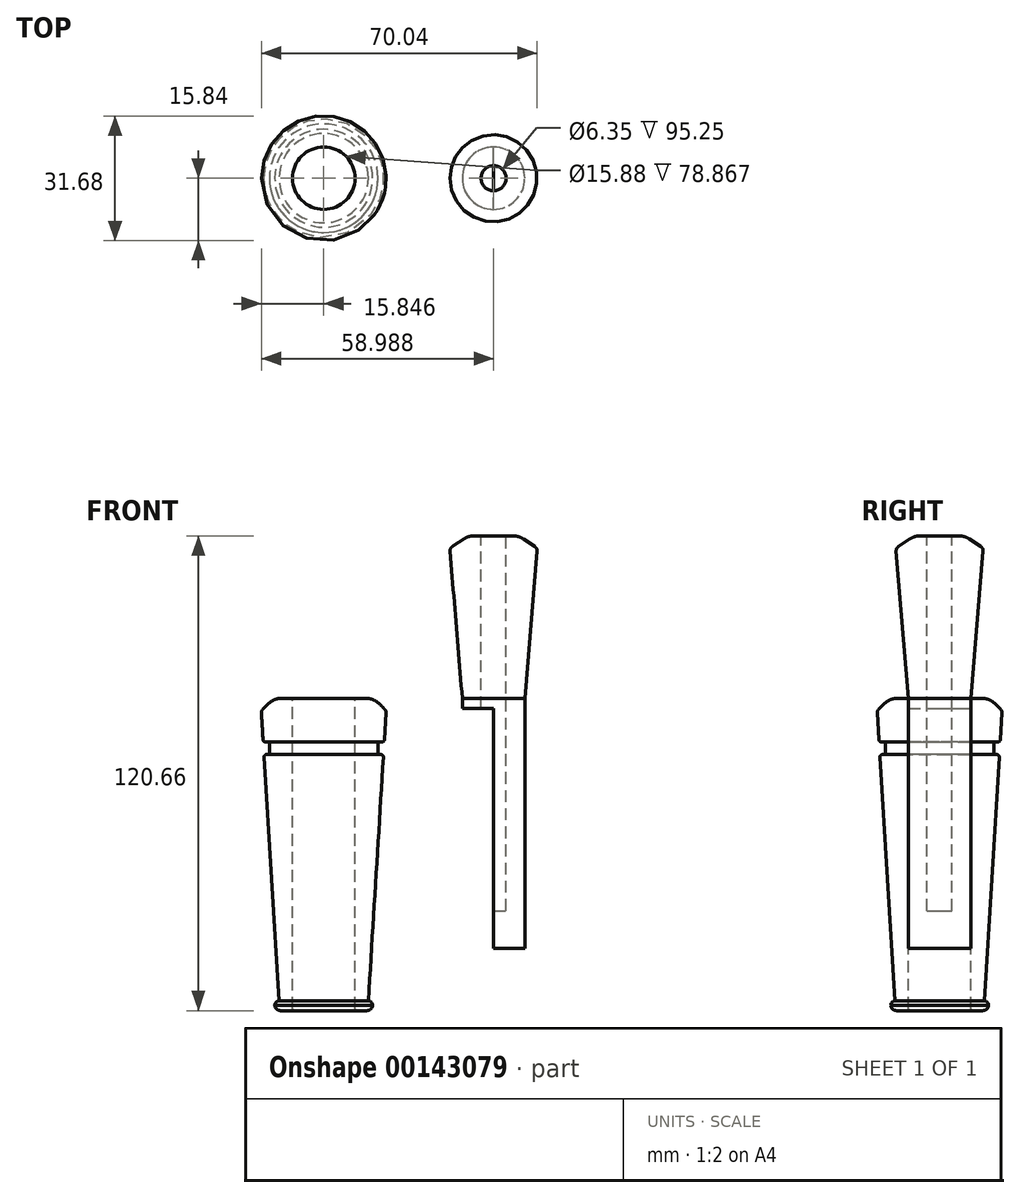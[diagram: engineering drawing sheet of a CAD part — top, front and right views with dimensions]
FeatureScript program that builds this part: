
annotation { "Feature Type Name" : "Feature", "Feature Type Description" : "" }
export const myFeature = defineFeature(function(context is Context, id is Id, definition is map)
    precondition{}
    {
        {
            var Q0;
            Q0=qCreatedBy(makeId("Front.planeOp"),FACE);
            var sketch = newSketch(context, id + "F0", { "sketchPlane" : qUnion([Q0])});
            skLineSegment(sketch, "E0", {"start": v(-45.17, -3.17) * mm, "end": v(-29.3, -3.17) * mm});
            skLineSegment(sketch, "E1", {"start": v(-29.3, -3.17) * mm, "end": v(-29.3, -79.38) * mm});
            skLineSegment(sketch, "E2", {"start": v(-29.3, -79.38) * mm, "end": v(-40.47, -79.38) * mm});
            skLineSegment(sketch, "E3", {"start": v(-45.17, -3.18) * mm, "end": v(-44.68, -11.11) * mm});
            skLineSegment(sketch, "E4", {"start": v(-40.47, -79.38) * mm, "end": v(-41.74, -79.38) * mm});
            skLineSegment(sketch, "E5", {"start": v(-41.74, -79.38) * mm, "end": v(-41.74, -76.83) * mm});
            skLineSegment(sketch, "E6", {"start": v(-41.74, -76.83) * mm, "end": v(-29.3, -76.83) * mm});
            skLineSegment(sketch, "E7", {"start": v(-29.3, -3.17) * mm, "end": v(-29.3, 0) * mm});
            skLineSegment(sketch, "E8", {"start": v(-29.3, 0) * mm, "end": v(-42, 0) * mm});
            skLineSegment(sketch, "E9", {"start": v(-42, 0) * mm, "end": v(-45.17, -3.18) * mm});
            skLineSegment(sketch, "E10", {"start": v(-29.3, -3.17) * mm, "end": v(-29.3, -12.7) * mm});
            skLineSegment(sketch, "E11", {"start": v(-29.3, -12.7) * mm, "end": v(-43.1, -12.7) * mm});
            skLineSegment(sketch, "E12", {"start": v(-44.68, -11.11) * mm, "end": v(-43.1, -11.11) * mm});
            skLineSegment(sketch, "E13", {"start": v(-44.48, -14.29) * mm, "end": v(-43.1, -14.29) * mm});
            skLineSegment(sketch, "E14", {"start": v(-43.1, -11.11) * mm, "end": v(-43.1, -14.29) * mm});
            skLineSegment(sketch, "E15.trimOffspring", {"start": v(-44.48, -14.29) * mm, "end": v(-40.47, -79.38) * mm});
            skLineSegment(sketch, "E16", {"start": v(-29.3, 6.8) * mm, "end": v(-37.23, 6.8) * mm, "construction": true});
            skLineSegment(sketch, "E17", {"start": v(-37.23, 6.8) * mm, "end": v(-37.23, -111.45) * mm, "construction": true});
            skLineSegment(sketch, "E18", {"start": v(-37.23, -76.83) * mm, "end": v(-40.63, -76.83) * mm, "construction": true});
            skSolve(sketch);
        }
        {
            var Q0;
            Q0=makeQuery(id+"F0.imprint","IMPRINT",FACE,{"disambiguationData":[TD([[makeQuery(id+"F0.imprint","IMPRINT",EDGE,{"derivedFrom":sQuery(id+"F0.wireOp",EDGE,"E0")}),1.0]])]});
            var Q1;
            Q1=makeQuery(id+"F0.imprint","IMPRINT",FACE,{"disambiguationData":[TD([[makeQuery(id+"F0.imprint","IMPRINT",EDGE,{"derivedFrom":sQuery(id+"F0.wireOp",EDGE,"E0")}),-1.0]])]});
            var Q2;
            {var subQ1=sQuery(id+"F0.wireOp",EDGE,"E11");Q2=makeQuery(id+"F0.imprint","IMPRINT",FACE,{"disambiguationData":[TD([[makeQuery(id+"F0.imprint","IMPRINT",EDGE,{"derivedFrom":subQ1}),1.0]])]});}
            var Q3;
            {var subQ0=sQuery(id+"F0.wireOp",EDGE,"E2");Q3=makeQuery(id+"F0.imprint","IMPRINT",FACE,{"disambiguationData":[TD([[makeQuery(id+"F0.imprint","IMPRINT",EDGE,{"derivedFrom":subQ0}),-1.0]])]});}
            var Q4;
            {var subQ0=sQuery(id+"F0.wireOp",EDGE,"E4");Q4=makeQuery(id+"F0.imprint","IMPRINT",FACE,{"disambiguationData":[TD([[makeQuery(id+"F0.imprint","IMPRINT",EDGE,{"derivedFrom":subQ0}),-1.0]])]});}
            var Q5;
            Q5=sQuery(id+"F0.wireOp",EDGE,"E1");
            revolve(context, id + "F1", {"entities" : qUnion([Q0, Q1, Q2, Q3, Q4]), "axis" : qUnion([Q5]), "revolveType" : RevolveType.FULL});
        }
        {
            var Q0;
            Q0=makeQuery(id+"F1.opRevolve","SWEPT_FACE",FACE,{"disambiguationData":[OSD([sQuery(id+"F0.wireOp",EDGE,"E8")])]});
            var sketch = newSketch(context, id + "F2", { "sketchPlane" : qUnion([Q0])});
            skCircle(sketch, "E19", {"center": v(-29.3, 0) * mm, "radius": 7.94 * mm});
            skSolve(sketch);
        }
        {
            var Q0;
            Q0 = qSketchRegion(id + "F2", true);
            extrude(context, id + "F3", {"entities" : qUnion([Q0]), "operationType" : NewBodyOperationType.REMOVE, "endBound" : BoundingType.THROUGH_ALL, "oppositeDirection" : true, "depth" : 25.4 * mm});
        }
        {
            var Q0;
            Q0=qCreatedBy(makeId("Front.planeOp"),FACE);
            var sketch = newSketch(context, id + "F4", { "sketchPlane" : qUnion([Q0])});
            skLineSegment(sketch, "E20", {"start": v(13.85, 0) * mm, "end": v(13.85, 38.1) * mm});
            skLineSegment(sketch, "E21", {"start": v(13.85, 38.1) * mm, "end": v(13.85, 41.27) * mm});
            skLineSegment(sketch, "E22", {"start": v(13.85, 41.27) * mm, "end": v(7.5, 41.27) * mm});
            skLineSegment(sketch, "E23", {"start": v(5.91, 0) * mm, "end": v(5.91, -63.5) * mm});
            skLineSegment(sketch, "E24", {"start": v(13.85, 0) * mm, "end": v(13.85, -63.5) * mm});
            skLineSegment(sketch, "E25", {"start": v(13.85, -63.5) * mm, "end": v(5.91, -63.5) * mm});
            skLineSegment(sketch, "E26", {"start": v(13.85, 38.1) * mm, "end": v(2.74, 38.1) * mm});
            skLineSegment(sketch, "E27", {"start": v(5.91, 0) * mm, "end": v(2.74, 38.1) * mm});
            skLineSegment(sketch, "E28", {"start": v(2.74, 38.1) * mm, "end": v(7.5, 41.27) * mm});
            skSolve(sketch);
        }
        {
            var Q0;
            Q0 = qSketchRegion(id + "F4", true);
            var Q1;
            Q1=sQuery(id+"F4.wireOp",EDGE,"E20");
            revolve(context, id + "F5", {"entities" : qUnion([Q0]), "axis" : qUnion([Q1]), "revolveType" : RevolveType.FULL});
        }
        {
            var Q0;
            Q0=makeQuery(id+"F5.opRevolve","SWEPT_FACE",FACE,{"disambiguationData":[OSD([sQuery(id+"F4.wireOp",EDGE,"E25")])]});
            var sketch = newSketch(context, id + "F6", { "sketchPlane" : qUnion([Q0])});
            skArc(sketch, "E29", {"start": v(13.85, 7.94) * mm, "mid": v(5.91, 0) * mm, "end": v(13.85, -7.94) * mm});
            skLineSegment(sketch, "E30", {"start": v(13.85, 7.94) * mm, "end": v(13.85, -7.94) * mm});
            skSolve(sketch);
        }
        {
            var Q0;
            Q0 = qSketchRegion(id + "F6", true);
            extrude(context, id + "F7", {"entities" : qUnion([Q0]), "operationType" : NewBodyOperationType.REMOVE, "oppositeDirection" : true, "depth" : 60.96 * mm});
        }
        {
            var Q0;
            Q0=makeQuery(id+"F5.opRevolve","SWEPT_FACE",FACE,{"disambiguationData":[OSD([sQuery(id+"F4.wireOp",EDGE,"E22")])]});
            var sketch = newSketch(context, id + "F8", { "sketchPlane" : qUnion([Q0])});
            skCircle(sketch, "E31", {"center": v(13.85, 0) * mm, "radius": 3.18 * mm});
            skSolve(sketch);
        }
        {
            var Q0;
            Q0 = qSketchRegion(id + "F8", true);
            extrude(context, id + "F9", {"entities" : qUnion([Q0]), "operationType" : NewBodyOperationType.REMOVE, "oppositeDirection" : true, "depth" : 95.25 * mm});
        }
        {
            var Q0;
            Q0=makeQuery(id+"F5.opRevolve","SWEPT_EDGE",EDGE,{"disambiguationData":[OSD([sQuery(id+"F4.wireOp",EDGE,"E22"),sQuery(id+"F4.wireOp",EDGE,"E28")])]});
            fillet(context, id + "F10", {"entities" : qUnion([Q0]), "radius" : 5.08 * mm, "tangentPropagation" : true, "allowEdgeOverflow" : false});
        }
        {
            var Q0;
            Q0=makeQuery(id+"F5.opRevolve","SWEPT_EDGE",EDGE,{"disambiguationData":[OSD([sQuery(id+"F4.wireOp",EDGE,"E26"),sQuery(id+"F4.wireOp",EDGE,"E27"),sQuery(id+"F4.wireOp",EDGE,"E28")])]});
            fillet(context, id + "F11", {"entities" : qUnion([Q0]), "radius" : 1.27 * mm, "tangentPropagation" : true, "allowEdgeOverflow" : false});
        }
        {
            var Q0;
            Q0=makeQuery(id+"F1.opRevolve","SWEPT_EDGE",EDGE,{"disambiguationData":[OSD([sQuery(id+"F0.wireOp",EDGE,"E8"),sQuery(id+"F0.wireOp",EDGE,"E9")])]});
            fillet(context, id + "F12", {"entities" : qUnion([Q0]), "radius" : 5.08 * mm, "tangentPropagation" : true, "allowEdgeOverflow" : false});
        }
        {
            var Q0;
            Q0=makeQuery(id+"F1.opRevolve","SWEPT_EDGE",EDGE,{"disambiguationData":[OSD([sQuery(id+"F0.wireOp",EDGE,"E0"),sQuery(id+"F0.wireOp",EDGE,"E3"),sQuery(id+"F0.wireOp",EDGE,"E9")])]});
            fillet(context, id + "F13", {"entities" : qUnion([Q0]), "radius" : 1.27 * mm, "tangentPropagation" : true, "allowEdgeOverflow" : false});
        }
        {
            var Q0;
            Q0=makeQuery(id+"F1.opRevolve","SWEPT_EDGE",EDGE,{"disambiguationData":[OSD([sQuery(id+"F0.wireOp",EDGE,"E13"),sQuery(id+"F0.wireOp",EDGE,"E15.trimOffspring")])]});
            var Q1;
            Q1=makeQuery(id+"F1.opRevolve","SWEPT_EDGE",EDGE,{"disambiguationData":[OSD([sQuery(id+"F0.wireOp",EDGE,"E3"),sQuery(id+"F0.wireOp",EDGE,"E12")])]});
            fillet(context, id + "F14", {"entities" : qUnion([Q0, Q1]), "radius" : 0.64 * mm, "tangentPropagation" : true, "allowEdgeOverflow" : false});
        }
        {
            var Q0;
            Q0=makeQuery(id+"F1.opRevolve","SWEPT_EDGE",EDGE,{"disambiguationData":[OSD([sQuery(id+"F0.wireOp",EDGE,"E13"),sQuery(id+"F0.wireOp",EDGE,"E14")])]});
            var Q1;
            {var subQ0=sQuery(id+"F0.wireOp",EDGE,"E12");Q1=makeQuery(id+"F14.opFillet","BLEND_EDGE",EDGE,{"blendedFrom":[makeQuery(id+"F1.opRevolve","SWEPT_EDGE",EDGE,{"disambiguationData":[OSD([sQuery(id+"F0.wireOp",EDGE,"E3"),subQ0])]}),makeQuery(id+"F1.opRevolve","SWEPT_FACE",FACE,{"disambiguationData":[OSD([subQ0])]})],"blendedInto":[makeQuery(id+"F1.opRevolve","SWEPT_FACE",FACE,{"disambiguationData":[OSD([subQ0])]})]});}
            fillet(context, id + "F15", {"entities" : qUnion([Q0, Q1]), "radius" : 0.64 * mm, "tangentPropagation" : true, "allowEdgeOverflow" : false});
        }
        {
            var Q0;
            Q0=makeQuery(id+"F1.opRevolve","SWEPT_EDGE",EDGE,{"disambiguationData":[OSD([sQuery(id+"F0.wireOp",EDGE,"E5"),sQuery(id+"F0.wireOp",EDGE,"E6")])]});
            fillet(context, id + "F16", {"entities" : qUnion([Q0]), "radius" : 1.27 * mm, "tangentPropagation" : true, "allowEdgeOverflow" : false});
        }
        {
            var Q0;
            Q0=makeQuery(id+"F1.opRevolve","SWEPT_EDGE",EDGE,{"disambiguationData":[OSD([sQuery(id+"F0.wireOp",EDGE,"E4"),sQuery(id+"F0.wireOp",EDGE,"E5")])]});
            fillet(context, id + "F17", {"entities" : qUnion([Q0]), "radius" : 1.52 * mm, "tangentPropagation" : true, "allowEdgeOverflow" : false});
        }
        {
            var Q0;
            Q0=makeQuery(id+"F3.boolean.opBoolean","INTERSECT",EDGE,{"derivedFrom":[makeQuery(id+"F1.opRevolve","SWEPT_FACE",FACE,{"disambiguationData":[OSD([sQuery(id+"F0.wireOp",EDGE,"E2"),sQuery(id+"F0.wireOp",EDGE,"E4")])]}),makeQuery(id+"F3.opExtrude","SWEPT_FACE",FACE,{"disambiguationData":[OSD([sQuery(id+"F2.wireOp",EDGE,"E19")])]})]});
            fillet(context, id + "F18", {"entities" : qUnion([Q0]), "radius" : 0.5 * mm, "tangentPropagation" : true, "allowEdgeOverflow" : false});
        }
    });
